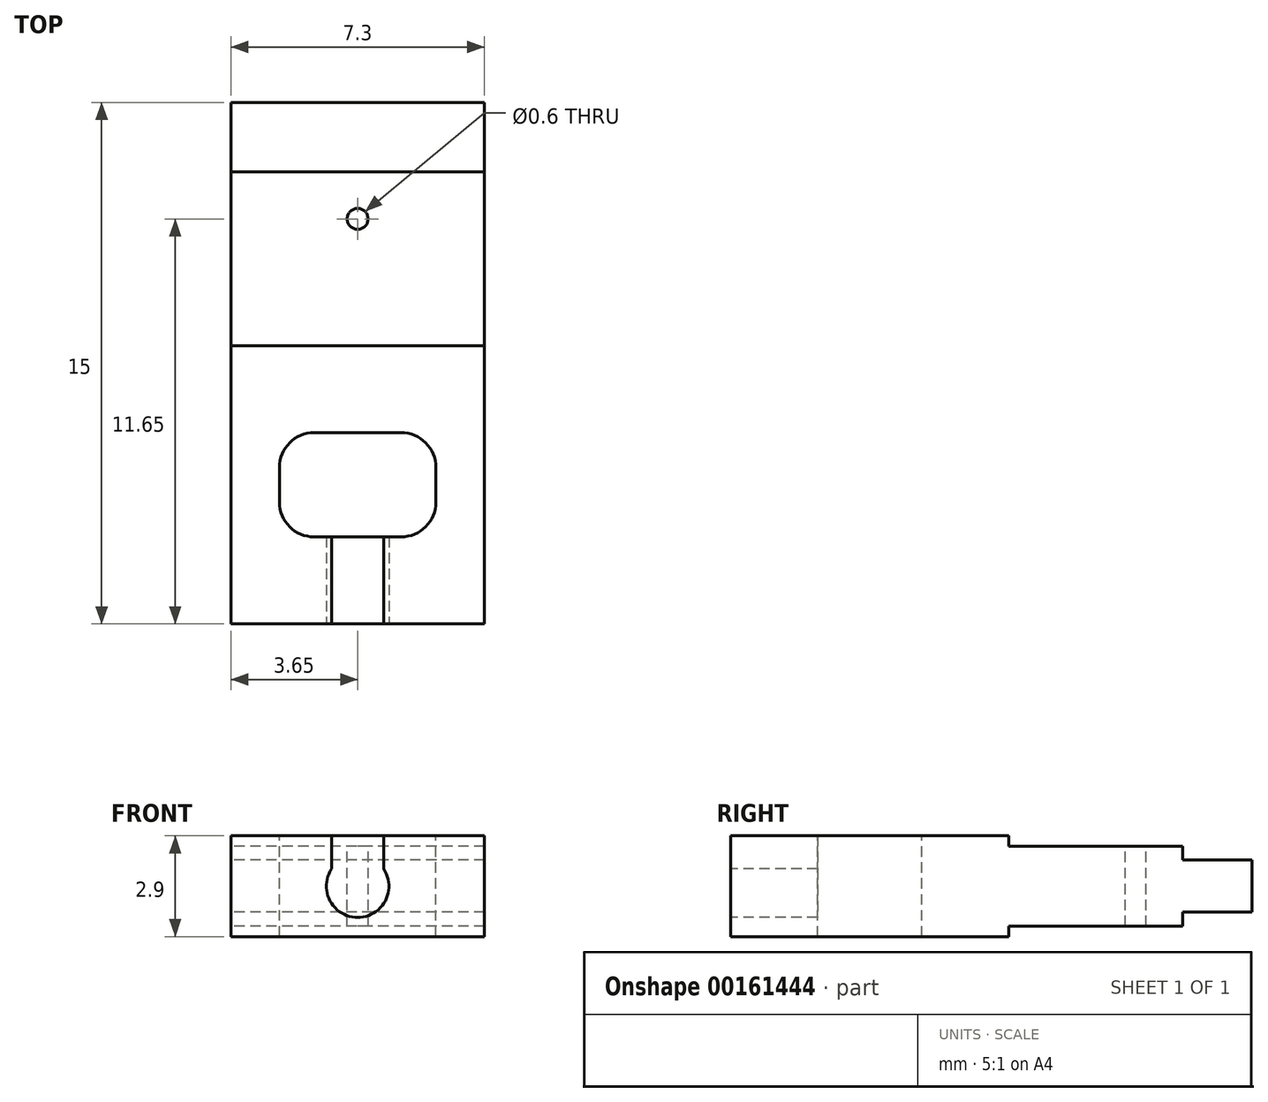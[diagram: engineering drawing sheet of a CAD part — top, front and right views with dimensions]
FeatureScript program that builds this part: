
annotation { "Feature Type Name" : "Feature", "Feature Type Description" : "" }
export const myFeature = defineFeature(function(context is Context, id is Id, definition is map)
    precondition{}
    {
        {
            assignVariable(context, id + "F0", {"name" : "Main_Width", "anyValue" : 7.3});
        }
        {
            var Q0;
            Q0=qCreatedBy(makeId("Right.planeOp"),FACE);
            var sketch = newSketch(context, id + "F1", { "sketchPlane" : qUnion([Q0])});
            skLineSegment(sketch, "E0", {"start": v(0, 0) * mm, "end": v(0, 1.45) * mm});
            skLineSegment(sketch, "E1", {"start": v(0, 1.45) * mm, "end": v(8, 1.45) * mm});
            skLineSegment(sketch, "E2", {"start": v(8, 1.45) * mm, "end": v(8, 1.15) * mm});
            skLineSegment(sketch, "E3", {"start": v(8, 1.15) * mm, "end": v(13, 1.15) * mm});
            skLineSegment(sketch, "E4", {"start": v(13, 1.15) * mm, "end": v(13, 0.75) * mm});
            skLineSegment(sketch, "E5", {"start": v(13, 0.75) * mm, "end": v(15, 0.75) * mm});
            skLineSegment(sketch, "E6", {"start": v(15, 0.75) * mm, "end": v(15, 0) * mm});
            skLineSegment(sketch, "E7", {"start": v(0, 0) * mm, "end": v(15, 0) * mm, "construction": true});
            skLineSegment(sketch, "E8.MirrorCS", {"start": v(0, -1.45) * mm, "end": v(8, -1.45) * mm});
            skLineSegment(sketch, "E9.MirrorCS", {"start": v(8, -1.45) * mm, "end": v(8, -1.15) * mm});
            skLineSegment(sketch, "E10.MirrorCS", {"start": v(0, 0) * mm, "end": v(0, -1.45) * mm});
            skLineSegment(sketch, "E11.MirrorCS", {"start": v(13, -0.75) * mm, "end": v(15, -0.75) * mm});
            skLineSegment(sketch, "E12.MirrorCS", {"start": v(15, -0.75) * mm, "end": v(15, 0) * mm});
            skLineSegment(sketch, "E13.MirrorCS", {"start": v(13, -1.15) * mm, "end": v(13, -0.75) * mm});
            skLineSegment(sketch, "E14.MirrorCS", {"start": v(8, -1.15) * mm, "end": v(13, -1.15) * mm});
            skSolve(sketch);
        }
        {
            var Q0;
            Q0=makeQuery(id+"F1.imprint","IMPRINT",FACE,{"disambiguationData":[TD([[makeQuery(id+"F1.imprint","IMPRINT",EDGE,{"derivedFrom":sQuery(id+"F1.wireOp",EDGE,"E0")}),-1.0]])]});
            extrude(context, id + "F2", {"entities" : qUnion([Q0]), "depth" : (getVariable(context, 'Main_Width')) * mm});
        }
        {
            var Q0;
            Q0=makeQuery(id+"F2.opExtrude","SWEPT_FACE",FACE,{"disambiguationData":[OSD([sQuery(id+"F1.wireOp",EDGE,"E1")])]});
            var sketch = newSketch(context, id + "F3", { "sketchPlane" : qUnion([Q0])});
            skCircle(sketch, "E15", {"center": v(3.65, 11.65) * mm, "radius": 0.3 * mm});
            skLineSegment(sketch, "E16.0", {"start": v(7.3, 0) * mm, "end": v(0, 0) * mm});
            skLineSegment(sketch, "E17", {"start": v(3.65, 11.65) * mm, "end": v(3.65, 0) * mm, "construction": true});
            skPoint(sketch, "E17.endSnap0", {"position": v(3.65, 0) * mm});
            skLineSegment(sketch, "E18.bottom", {"start": v(2.4, 2.5) * mm, "end": v(4.9, 2.5) * mm});
            skLineSegment(sketch, "E18.top", {"start": v(2.4, 5.5) * mm, "end": v(4.9, 5.5) * mm});
            skLineSegment(sketch, "E18.left", {"start": v(2.4, 2.5) * mm, "end": v(2.4, 5.5) * mm, "construction": true});
            skLineSegment(sketch, "E18.right", {"start": v(4.9, 2.5) * mm, "end": v(4.9, 5.5) * mm, "construction": true});
            skPoint(sketch, "E18.middle", {"position": v(3.65, 4) * mm});
            skArc(sketch, "E19", {"start": v(1.4, 3.5) * mm, "mid": v(1.7, 2.8) * mm, "end": v(2.4, 2.5) * mm});
            skArc(sketch, "E20", {"start": v(2.4, 5.5) * mm, "mid": v(1.7, 5.2) * mm, "end": v(1.4, 4.5) * mm});
            skLineSegment(sketch, "E21", {"start": v(1.4, 3.5) * mm, "end": v(1.4, 4.5) * mm});
            skArc(sketch, "E22.MirrorCS", {"start": v(4.9, 5.5) * mm, "mid": v(5.6, 5.2) * mm, "end": v(5.9, 4.5) * mm});
            skLineSegment(sketch, "E23.MirrorCS", {"start": v(5.9, 3.5) * mm, "end": v(5.9, 4.5) * mm});
            skArc(sketch, "E24.MirrorCS", {"start": v(5.9, 3.5) * mm, "mid": v(5.6, 2.8) * mm, "end": v(4.9, 2.5) * mm});
            skSolve(sketch);
        }
        {
            var Q0;
            Q0=makeQuery(id+"F3.imprint","IMPRINT",FACE,{"disambiguationData":[TD([[makeQuery(id+"F3.imprint","IMPRINT",EDGE,{"derivedFrom":sQuery(id+"F3.wireOp",EDGE,"E18.bottom")}),1.0]])]});
            var Q1;
            Q1=makeQuery(id+"F3.imprint","IMPRINT",FACE,{"disambiguationData":[TD([[makeQuery(id+"F3.imprint","IMPRINT",EDGE,{"derivedFrom":sQuery(id+"F3.wireOp",EDGE,"E15")}),1.0]])]});
            extrude(context, id + "F4", {"entities" : qUnion([Q0, Q1]), "operationType" : NewBodyOperationType.REMOVE, "endBound" : BoundingType.THROUGH_ALL, "oppositeDirection" : true, "depth" : 25 * mm});
        }
        {
            var Q0;
            Q0=makeQuery(id+"F2.opExtrude","SWEPT_FACE",FACE,{"disambiguationData":[OSD([sQuery(id+"F1.wireOp",EDGE,"E0"),sQuery(id+"F1.wireOp",EDGE,"E10.MirrorCS")])]});
            var sketch = newSketch(context, id + "F5", { "sketchPlane" : qUnion([Q0])});
            skLineSegment(sketch, "E25.0.0", {"start": v(0, 1.45) * mm, "end": v(0, -1.45) * mm});
            skLineSegment(sketch, "E25.0.1", {"start": v(0, -1.45) * mm, "end": v(7.3, -1.45) * mm});
            skLineSegment(sketch, "E25.0.2", {"start": v(7.3, -1.45) * mm, "end": v(7.3, 1.45) * mm});
            skLineSegment(sketch, "E25.0.3", {"start": v(7.3, 1.45) * mm, "end": v(0, 1.45) * mm});
            skArc(sketch, "E26", {"start": v(2.9, 0.5) * mm, "mid": v(3.65, -0.9) * mm, "end": v(4.4, 0.5) * mm});
            skLineSegment(sketch, "E27", {"start": v(3.65, 1.45) * mm, "end": v(3.65, -1.45) * mm, "construction": true});
            skLineSegment(sketch, "E28", {"start": v(2.9, 0.5) * mm, "end": v(2.9, 1.45) * mm});
            skLineSegment(sketch, "E29", {"start": v(4.4, 0.5) * mm, "end": v(4.4, 1.45) * mm});
            skSolve(sketch);
        }
        {
            var Q0;
            Q0=makeQuery(id+"F5.imprint","IMPRINT",FACE,{"disambiguationData":[TD([[makeQuery(id+"F5.imprint","IMPRINT",EDGE,{"derivedFrom":sQuery(id+"F5.wireOp",EDGE,"E26")}),1.0]])]});
            extrude(context, id + "F6", {"entities" : qUnion([Q0]), "operationType" : NewBodyOperationType.REMOVE, "endBound" : BoundingType.UP_TO_NEXT, "oppositeDirection" : true, "depth" : 25 * mm});
        }
    });
